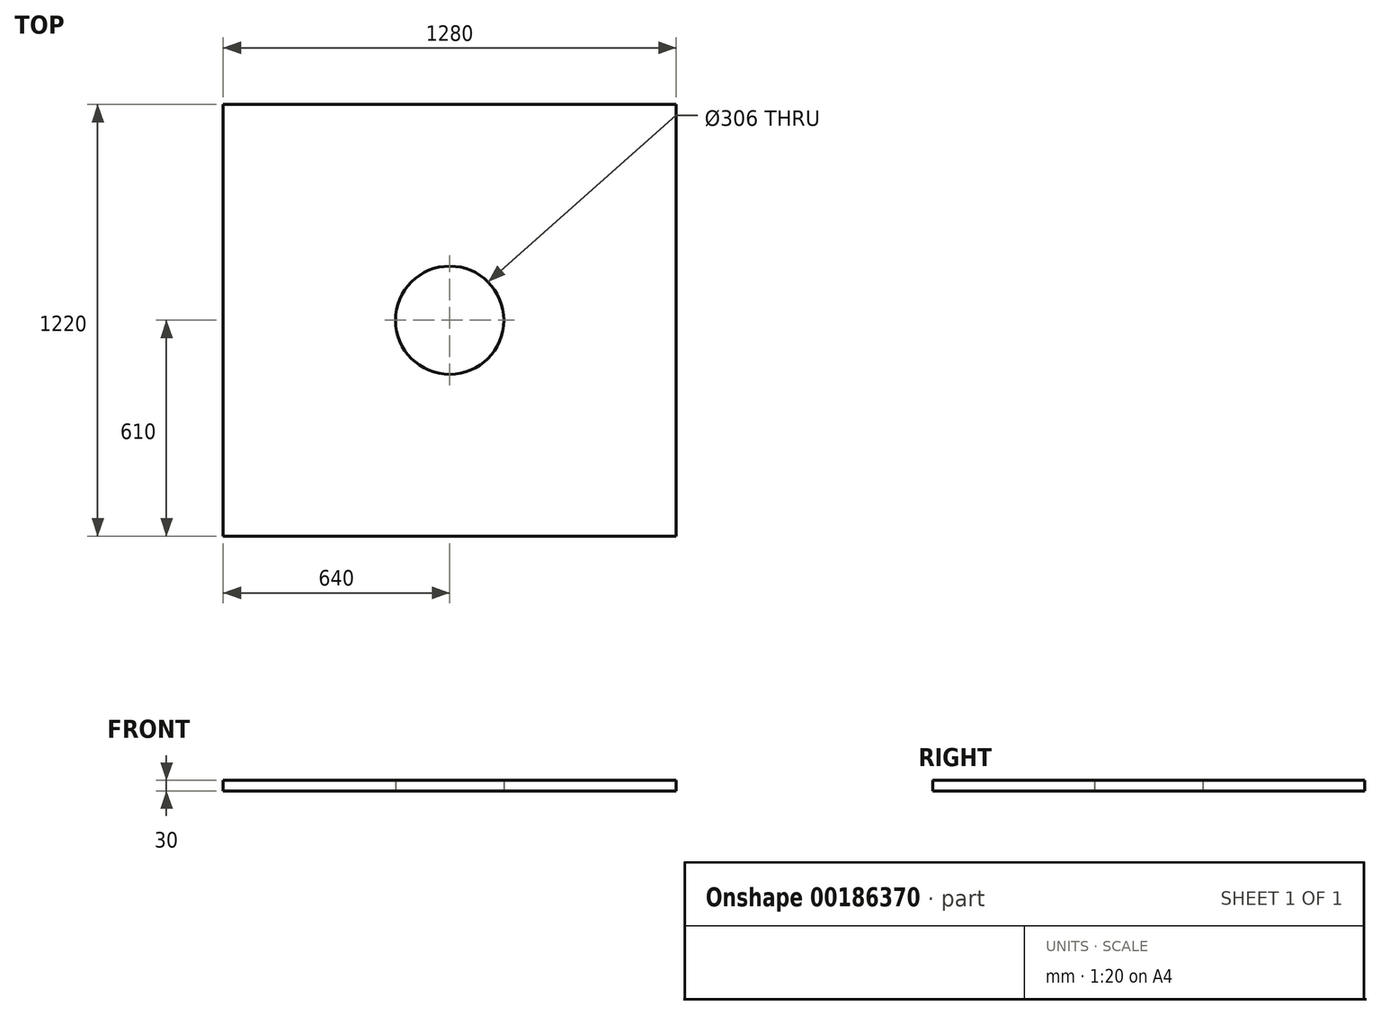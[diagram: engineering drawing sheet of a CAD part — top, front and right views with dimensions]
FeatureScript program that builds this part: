
annotation { "Feature Type Name" : "Feature", "Feature Type Description" : "" }
export const myFeature = defineFeature(function(context is Context, id is Id, definition is map)
    precondition{}
    {
        {
            var Q0;
            Q0=qCreatedBy(makeId("Top.planeOp"),FACE);
            var sketch = newSketch(context, id + "F0", { "sketchPlane" : qUnion([Q0])});
            skLineSegment(sketch, "E0.bottom", {"start": v(-1280, 1220) * mm, "end": v(0, 1220) * mm});
            skLineSegment(sketch, "E0.top", {"start": v(-1280, 0) * mm, "end": v(0, 0) * mm});
            skLineSegment(sketch, "E0.left", {"start": v(-1280, 1220) * mm, "end": v(-1280, 0) * mm});
            skLineSegment(sketch, "E0.right", {"start": v(0, 1220) * mm, "end": v(0, 0) * mm});
            skCircle(sketch, "E1", {"center": v(-640, 610) * mm, "radius": 153 * mm});
            skLineSegment(sketch, "E2", {"start": v(-640, 610) * mm, "end": v(-640, 0) * mm, "construction": true});
            skLineSegment(sketch, "E3", {"start": v(-640, 610) * mm, "end": v(0, 610) * mm, "construction": true});
            skSolve(sketch);
        }
        {
            var Q0;
            Q0 = qSketchRegion(id + "F0", true);
            extrude(context, id + "F1", {"entities" : qUnion([Q0]), "depth" : 30 * mm});
        }
    });
